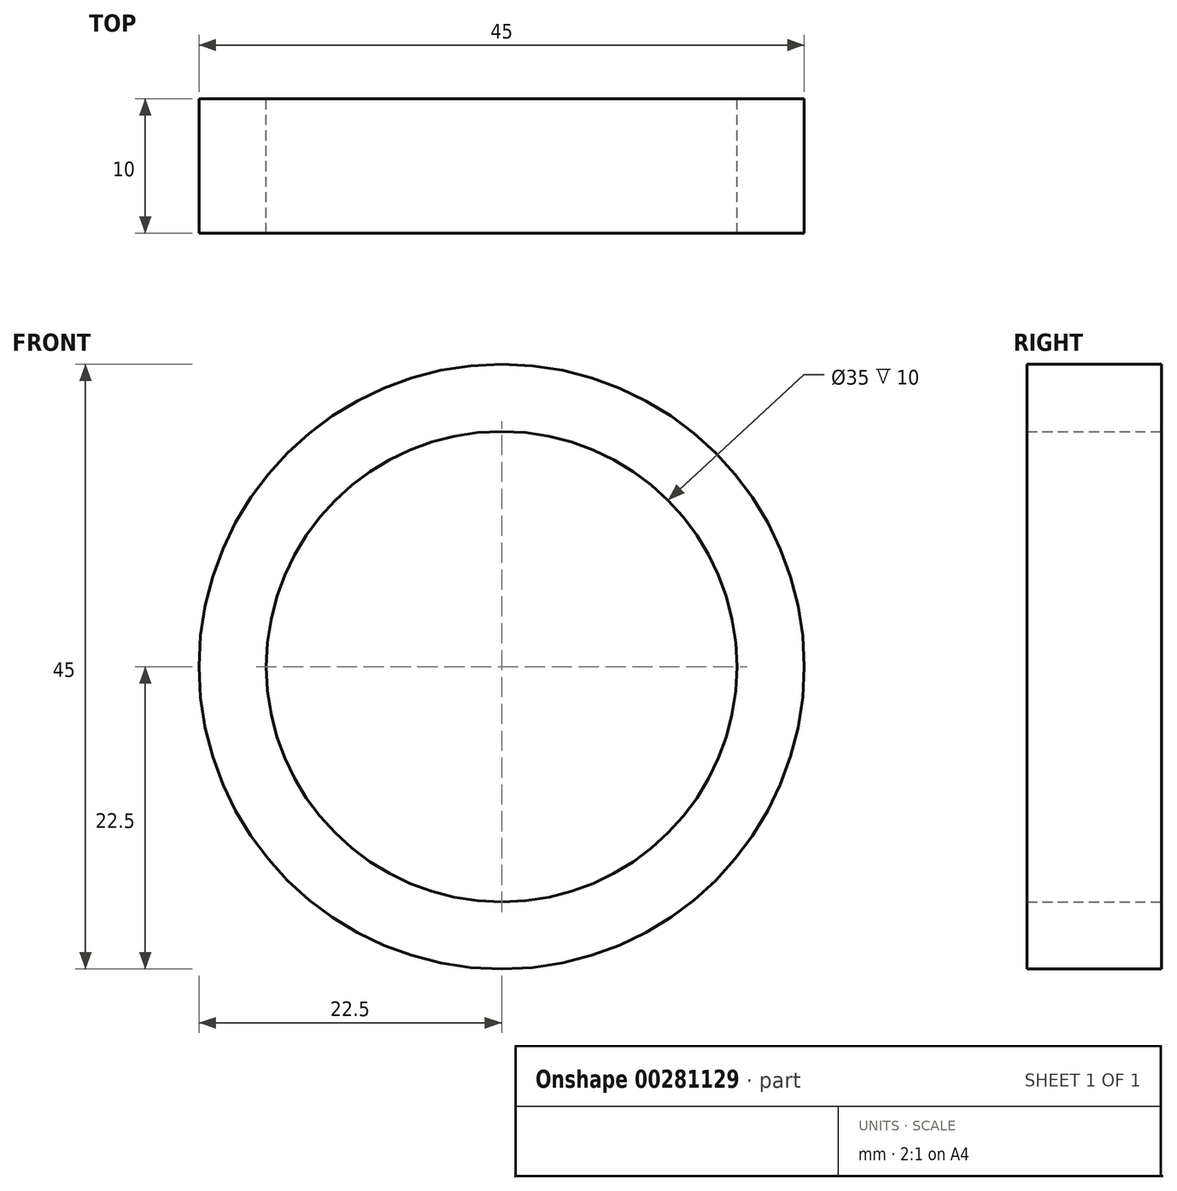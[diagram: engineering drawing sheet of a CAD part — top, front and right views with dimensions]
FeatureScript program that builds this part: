
annotation { "Feature Type Name" : "Feature", "Feature Type Description" : "" }
export const myFeature = defineFeature(function(context is Context, id is Id, definition is map)
    precondition{}
    {
        {
            var Q0;
            Q0=qCreatedBy(makeId("Front.planeOp"),FACE);
            var sketch = newSketch(context, id + "F0", { "sketchPlane" : qUnion([Q0])});
            skCircle(sketch, "E0", {"center": v(0, 0) * mm, "radius": 17.5 * mm});
            skCircle(sketch, "E1", {"center": v(0, 0) * mm, "radius": 22.5 * mm});
            skSolve(sketch);
        }
        {
            var Q0;
            Q0=makeQuery(id+"F0.imprint","IMPRINT",FACE,{"disambiguationData":[TD([[makeQuery(id+"F0.imprint","IMPRINT",EDGE,{"derivedFrom":sQuery(id+"F0.wireOp",EDGE,"E0")}),-1.0]])]});
            extrude(context, id + "F1", {"entities" : qUnion([Q0]), "depth" : 10 * mm});
        }
    });
